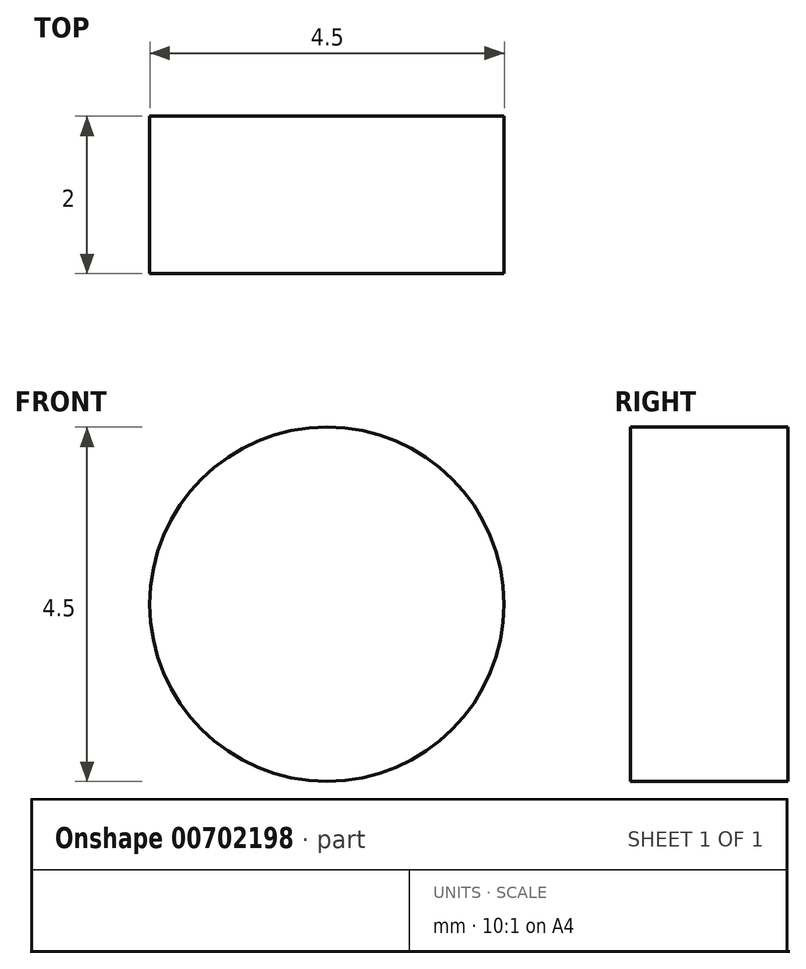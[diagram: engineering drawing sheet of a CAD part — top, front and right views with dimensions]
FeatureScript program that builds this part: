
annotation { "Feature Type Name" : "Feature", "Feature Type Description" : "" }
export const myFeature = defineFeature(function(context is Context, id is Id, definition is map)
    precondition{}
    {
        {
            var Q0;
            Q0=qCreatedBy(makeId("Front.planeOp"),FACE);
            var sketch = newSketch(context, id + "F0", { "sketchPlane" : qUnion([Q0])});
            skLineSegment(sketch, "E0.bottom", {"start": v(147.07, -117.5) * mm, "end": v(-72.93, -117.5) * mm});
            skLineSegment(sketch, "E0.top", {"start": v(147.07, 117.5) * mm, "end": v(-72.93, 117.5) * mm});
            skLineSegment(sketch, "E0.left", {"start": v(147.07, -117.5) * mm, "end": v(147.07, 117.5) * mm});
            skPoint(sketch, "E0.middle", {"position": v(0, 0) * mm});
            skArc(sketch, "E1", {"start": v(-175.43, -15) * mm, "mid": v(-160.43, 0) * mm, "end": v(-175.43, 15) * mm});
            skLineSegment(sketch, "E2", {"start": v(-72.93, 117.5) * mm, "end": v(-175.43, 15) * mm});
            skLineSegment(sketch, "E3", {"start": v(-175.43, -15) * mm, "end": v(-72.93, -117.5) * mm});
            skSolve(sketch);
        }
        {
            var Q0;
            Q0=makeQuery(id+"F0.imprint","IMPRINT",FACE,{"disambiguationData":[TD([[makeQuery(id+"F0.imprint","IMPRINT",EDGE,{"derivedFrom":sQuery(id+"F0.wireOp",EDGE,"E0.bottom")}),-1.0]])]});
            extrude(context, id + "F1", {"entities" : qUnion([Q0]), "depth" : 2 * mm, "offsetDistance" : 25 * mm});
        }
        {
            var Q0;
            Q0=makeQuery(id+"F1.opExtrude","CAP_FACE",FACE,{"disambiguationData":[OSD([sQuery(id+"F0.wireOp",EDGE,"E0.bottom"),sQuery(id+"F0.wireOp",EDGE,"E0.top"),sQuery(id+"F0.wireOp",EDGE,"E0.left"),sQuery(id+"F0.wireOp",EDGE,"E1"),sQuery(id+"F0.wireOp",EDGE,"E2"),sQuery(id+"F0.wireOp",EDGE,"E3")])],"isStart":false});
            var sketch = newSketch(context, id + "F2", { "sketchPlane" : qUnion([Q0])});
            skLineSegment(sketch, "E4.bottom", {"start": v(80.32, -4.25) * mm, "end": v(68.82, -4.25) * mm});
            skLineSegment(sketch, "E4.top", {"start": v(80.32, 4.25) * mm, "end": v(68.82, 4.25) * mm});
            skPoint(sketch, "E4.middle", {"position": v(74.57, 0) * mm});
            skArc(sketch, "E5", {"start": v(68.82, 4.25) * mm, "mid": v(64.57, 0) * mm, "end": v(68.82, -4.25) * mm});
            skArc(sketch, "E6", {"start": v(80.32, -4.25) * mm, "mid": v(84.57, 0) * mm, "end": v(80.32, 4.25) * mm});
            skCircle(sketch, "E7", {"center": v(57.07, -112.5) * mm, "radius": 2.25 * mm});
            skCircle(sketch, "E8.MirrorC", {"center": v(57.07, 112.5) * mm, "radius": 2.25 * mm});
            skSolve(sketch);
        }
        {
            var Q0;
            Q0=makeQuery(id+"F2.imprint","IMPRINT",FACE,{"disambiguationData":[TD([[makeQuery(id+"F2.imprint","IMPRINT",EDGE,{"derivedFrom":sQuery(id+"F2.wireOp",EDGE,"E4.bottom")}),-1.0]])]});
            var Q1;
            Q1=makeQuery(id+"F2.imprint","IMPRINT",FACE,{"disambiguationData":[TD([[makeQuery(id+"F2.imprint","IMPRINT",EDGE,{"derivedFrom":sQuery(id+"F2.wireOp",EDGE,"E7")}),1.0]])]});
            var Q2;
            Q2=makeQuery(id+"F2.imprint","IMPRINT",FACE,{"disambiguationData":[TD([[makeQuery(id+"F2.imprint","IMPRINT",EDGE,{"derivedFrom":sQuery(id+"F2.wireOp",EDGE,"E8.MirrorC")}),-1.0]])]});
            extrude(context, id + "F3", {"entities" : qUnion([Q0, Q1, Q2]), "operationType" : NewBodyOperationType.REMOVE, "endBound" : BoundingType.UP_TO_NEXT, "oppositeDirection" : true, "depth" : 25 * mm, "offsetDistance" : 25 * mm});
        }
    });
